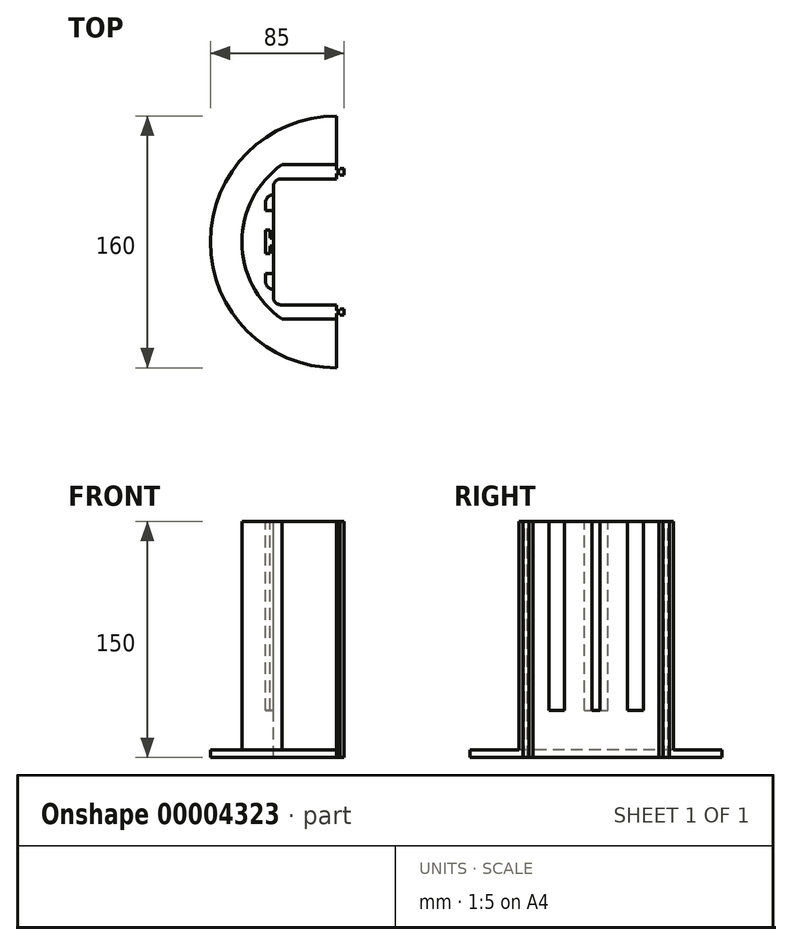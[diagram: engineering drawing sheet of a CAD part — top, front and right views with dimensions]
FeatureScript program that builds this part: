
annotation { "Feature Type Name" : "Feature", "Feature Type Description" : "" }
export const myFeature = defineFeature(function(context is Context, id is Id, definition is map)
    precondition{}
    {
        {
            var Q0;
            Q0=qCreatedBy(makeId("Top.planeOp"),FACE);
            var sketch = newSketch(context, id + "F0", { "sketchPlane" : qUnion([Q0])});
            skArc(sketch, "E0", {"start": v(0, 80) * mm, "mid": v(-80, 0) * mm, "end": v(0, -80) * mm});
            skLineSegment(sketch, "E1", {"start": v(0, -80) * mm, "end": v(0, 80) * mm});
            skLineSegment(sketch, "E2.0", {"start": v(-40, -35) * mm, "end": v(-40, 35) * mm});
            skLineSegment(sketch, "E3", {"start": v(-40, -80) * mm, "end": v(0, -80) * mm});
            skLineSegment(sketch, "E4.2", {"start": v(-43.15, -34.71) * mm, "end": v(-43.15, -34.34) * mm});
            skPoint(sketch, "E5.orphan", {"position": v(0, 60) * mm});
            skLineSegment(sketch, "E6.trimOffspring", {"start": v(-43.15, 34.91) * mm, "end": v(-43.15, 35.29) * mm});
            skLineSegment(sketch, "E7.0", {"start": v(-35, -40) * mm, "end": v(0, -40) * mm});
            skLineSegment(sketch, "E8.0", {"start": v(-35, -49) * mm, "end": v(0, -49) * mm});
            skArc(sketch, "E9.0", {"start": v(-34.63, 49) * mm, "mid": v(-60, 0) * mm, "end": v(-34.63, -49) * mm});
            skLineSegment(sketch, "E10.0", {"start": v(0, 40) * mm, "end": v(-35, 40) * mm});
            skLineSegment(sketch, "E11.0", {"start": v(0, 49) * mm, "end": v(-35, 49) * mm});
            skPoint(sketch, "E12.visualSharp", {"position": v(-40, 40) * mm});
            skArc(sketch, "E12.filletArc", {"start": v(-35, 40) * mm, "mid": v(-38.54, 38.54) * mm, "end": v(-40, 35) * mm});
            skPoint(sketch, "E13.visualSharp", {"position": v(-40, -40) * mm});
            skArc(sketch, "E13.filletArc", {"start": v(-40, -35) * mm, "mid": v(-38.54, -38.54) * mm, "end": v(-35, -40) * mm});
            skSolve(sketch);
        }
        {
            var Q0;
            {var subQ5=sQuery(id+"F0.wireOp",EDGE,"75c2bebc-5728-42c0-99f1-8c9a0116536a.0");Q0=makeQuery(id+"F0.imprint","IMPRINT",FACE,{"disambiguationData":[TD([[makeQuery(id+"F0.imprint","IMPRINT",EDGE,{"derivedFrom":subQ5}),-1.0]])]});}
            var Q1;
            {var subQ1=sQuery(id+"F0.wireOp",EDGE,"E2.0");var subQ5=makeQuery(id+"F0.imprint","INTERSECT",VERTEX,{"derivedFrom":[subQ1,sQuery(id+"F0.wireOp",EDGE,"75c2bebc-5728-42c0-99f1-8c9a0116536a.0")]});Q1=makeQuery(id+"F0.imprint","IMPRINT",FACE,{"disambiguationData":[TD([[makeQuery(id+"F0.imprint","IMPRINT",EDGE,{"disambiguationData":[TD([[subQ5,1.0]])],"derivedFrom":subQ1}),1.0]])]});}
            var Q2;
            {var subQ0=sQuery(id+"F0.wireOp",EDGE,"6f7f12fe-7da2-44be-81c8-f102f9fe9926.0");Q2=makeQuery(id+"F0.imprint","IMPRINT",FACE,{"disambiguationData":[TD([[makeQuery(id+"F0.imprint","IMPRINT",EDGE,{"derivedFrom":subQ0}),-1.0]])]});}
            extrude(context, id + "F1", {"entities" : qUnion([Q0, Q1, Q2]), "oppositeDirection" : true, "depth" : 150 * mm});
        }
        {
            var Q0;
            Q0=makeQuery(id+"F1.opExtrude","CAP_FACE",FACE,{"disambiguationData":[OSD([sQuery(id+"F0.wireOp",EDGE,"E1"),sQuery(id+"F0.wireOp",EDGE,"E2.0"),sQuery(id+"F0.wireOp",EDGE,"75c2bebc-5728-42c0-99f1-8c9a0116536a.0"),sQuery(id+"F0.wireOp",EDGE,"6f7f12fe-7da2-44be-81c8-f102f9fe9926.0"),sQuery(id+"F0.wireOp",EDGE,"6ea0f182-5685-4d39-b26f-b4a1ce07e50b.0")])],"isStart":false});
            var sketch = newSketch(context, id + "F2", { "sketchPlane" : qUnion([Q0])});
            skLineSegment(sketch, "E14", {"start": v(0, 40) * mm, "end": v(0, -80) * mm});
            skLineSegment(sketch, "E15", {"start": v(0, 40) * mm, "end": v(0, 80) * mm});
            skArc(sketch, "E16", {"start": v(0, 80) * mm, "mid": v(-80, 0) * mm, "end": v(0, -80) * mm});
            skSolve(sketch);
        }
        {
            var Q0;
            {var subQ2=sQuery(id+"F2.wireOp",EDGE,"E16");Q0=makeQuery(id+"F2.imprint","IMPRINT",FACE,{"disambiguationData":[TD([[makeQuery(id+"F2.imprint","IMPRINT",EDGE,{"derivedFrom":subQ2}),1.0]])]});}
            extrude(context, id + "F3", {"entities" : qUnion([Q0]), "operationType" : NewBodyOperationType.ADD, "oppositeDirection" : true, "depth" : 5 * mm});
        }
        {
            var Q0;
            Q0=makeQuery(id+"F1.opExtrude","CAP_FACE",FACE,{"disambiguationData":[OSD([sQuery(id+"F0.wireOp",EDGE,"E1"),sQuery(id+"F0.wireOp",EDGE,"E2.0"),sQuery(id+"F0.wireOp",EDGE,"75c2bebc-5728-42c0-99f1-8c9a0116536a.0"),sQuery(id+"F0.wireOp",EDGE,"6f7f12fe-7da2-44be-81c8-f102f9fe9926.0"),sQuery(id+"F0.wireOp",EDGE,"6ea0f182-5685-4d39-b26f-b4a1ce07e50b.0"),sQuery(id+"F0.wireOp",EDGE,"e7ebfef1-af54-467c-9f28-ac26729f73ad.filletArc"),sQuery(id+"F0.wireOp",EDGE,"8241e0cd-7dbd-4ec0-b380-70d9f552f549.filletArc")])],"isStart":true});
            var sketch = newSketch(context, id + "F4", { "sketchPlane" : qUnion([Q0])});
            skLineSegment(sketch, "E17", {"start": v(0, -40) * mm, "end": v(5, -40) * mm});
            skLineSegment(sketch, "E18", {"start": v(0, 40) * mm, "end": v(5, 40) * mm});
            skLineSegment(sketch, "E19.0", {"start": v(0, 43.5) * mm, "end": v(2.5, 43.5) * mm});
            skLineSegment(sketch, "E20.0", {"start": v(0, 45.5) * mm, "end": v(2.5, 45.5) * mm});
            skLineSegment(sketch, "E21", {"start": v(5, 45.5) * mm, "end": v(5, 43.5) * mm});
            skLineSegment(sketch, "E22.0", {"start": v(0, 45.5) * mm, "end": v(0, 43.5) * mm});
            skLineSegment(sketch, "E23", {"start": v(5, 45.5) * mm, "end": v(5, 46.5) * mm});
            skLineSegment(sketch, "E24", {"start": v(5, 43.5) * mm, "end": v(5, 42.5) * mm});
            skLineSegment(sketch, "E25.0", {"start": v(2.5, 45.5) * mm, "end": v(2.5, 46.5) * mm});
            skLineSegment(sketch, "E25.2", {"start": v(2.5, 43.5) * mm, "end": v(2.5, 42.5) * mm});
            skLineSegment(sketch, "E26", {"start": v(5, 42.5) * mm, "end": v(2.5, 42.5) * mm});
            skLineSegment(sketch, "E27", {"start": v(2.5, 46.5) * mm, "end": v(5, 46.5) * mm});
            skLineSegment(sketch, "E28.0", {"start": v(0, -45.5) * mm, "end": v(2.5, -45.5) * mm});
            skLineSegment(sketch, "E29.0", {"start": v(0, -43.5) * mm, "end": v(2.5, -43.5) * mm});
            skLineSegment(sketch, "E30", {"start": v(5, -43.5) * mm, "end": v(5, -45.5) * mm});
            skLineSegment(sketch, "E31", {"start": v(5, -43.5) * mm, "end": v(5, -42.5) * mm});
            skLineSegment(sketch, "E32", {"start": v(5, -45.5) * mm, "end": v(5, -46.5) * mm});
            skLineSegment(sketch, "E33.0", {"start": v(2.5, -43.5) * mm, "end": v(2.5, -42.5) * mm});
            skLineSegment(sketch, "E33.2", {"start": v(2.5, -45.5) * mm, "end": v(2.5, -46.5) * mm});
            skLineSegment(sketch, "E34", {"start": v(5, -42.5) * mm, "end": v(2.5, -42.5) * mm});
            skLineSegment(sketch, "E35", {"start": v(5, -46.5) * mm, "end": v(2.5, -46.5) * mm});
            skSolve(sketch);
        }
        {
            var Q0;
            Q0=makeQuery(id+"F4.imprint","IMPRINT",FACE,{"disambiguationData":[TD([[makeQuery(id+"F4.imprint","IMPRINT",EDGE,{"derivedFrom":sQuery(id+"F4.wireOp",EDGE,"E19.0")}),1.0]])]});
            var Q1;
            {var subQ3=sQuery(id+"F4.wireOp",EDGE,"E28.0");Q1=makeQuery(id+"F4.imprint","IMPRINT",FACE,{"disambiguationData":[TD([[makeQuery(id+"F4.imprint","IMPRINT",EDGE,{"derivedFrom":subQ3}),1.0]])]});}
            extrude(context, id + "F5", {"entities" : qUnion([Q0, Q1]), "operationType" : NewBodyOperationType.ADD, "oppositeDirection" : true, "depth" : 150 * mm});
        }
        {
            var Q0;
            {var subQ0=sQuery(id+"F0.wireOp",EDGE,"E1");Q0=makeQuery(id+"F5.boolean.opBoolean","MERGE",FACE,{"derivedFrom":[makeQuery(id+"F1.opExtrude","CAP_FACE",FACE,{"disambiguationData":[OSD([subQ0,sQuery(id+"F0.wireOp",EDGE,"E2.0"),sQuery(id+"F0.wireOp",EDGE,"75c2bebc-5728-42c0-99f1-8c9a0116536a.0"),sQuery(id+"F0.wireOp",EDGE,"6f7f12fe-7da2-44be-81c8-f102f9fe9926.0"),sQuery(id+"F0.wireOp",EDGE,"6ea0f182-5685-4d39-b26f-b4a1ce07e50b.0"),sQuery(id+"F0.wireOp",EDGE,"e7ebfef1-af54-467c-9f28-ac26729f73ad.filletArc"),sQuery(id+"F0.wireOp",EDGE,"8241e0cd-7dbd-4ec0-b380-70d9f552f549.filletArc")])],"isStart":true}),makeQuery(id+"F5.opExtrude","CAP_FACE",FACE,{"disambiguationData":[OSD([sQuery(id+"F4.wireOp",EDGE,"afc29b5e-58cc-4c7b-a192-24bd55086143.0"),sQuery(id+"F4.wireOp",EDGE,"29f716cb-9728-41fc-a06d-da8974d49b97.0"),sQuery(id+"F4.wireOp",EDGE,"28a342e1-f6da-4660-be7d-c49b4d0e2a07"),sQuery(id+"F4.wireOp",EDGE,"23a93fd6-abec-4492-8de1-6d2303d71052.0"),sQuery(id+"F4.wireOp",EDGE,"97a3bef3-9aef-4252-a859-6bd18b588f87"),sQuery(id+"F4.wireOp",EDGE,"a65524c8-dac2-4c7d-890a-83aa3edf8c0d"),sQuery(id+"F4.wireOp",EDGE,"3f23ce79-a299-4ef1-861a-d1ed6e96b0e4.0"),sQuery(id+"F4.wireOp",EDGE,"20cd2892-1dbe-4ddd-b802-98d3355a453f.0"),sQuery(id+"F4.wireOp",EDGE,"12dbb6a1-9dd6-4ab8-8469-4905e3c74d78"),sQuery(id+"F4.wireOp",EDGE,"0f2de19d-25e8-473d-b9a4-17b5fc715538")])],"isStart":true}),makeQuery(id+"F5.opExtrude","CAP_FACE",FACE,{"disambiguationData":[OSD([subQ0,sQuery(id+"F4.wireOp",EDGE,"73ee2f29-bcec-40ac-88de-c9b1e0e0407e.0"),sQuery(id+"F4.wireOp",EDGE,"760f6a40-cbb3-4914-97d4-89d93c9b81f9.0"),sQuery(id+"F4.wireOp",EDGE,"a534df8f-d272-4bc9-bed5-e4d40ce864a1"),sQuery(id+"F4.wireOp",EDGE,"6b7fad69-a33e-43b3-a84d-1ef3c3cb7823"),sQuery(id+"F4.wireOp",EDGE,"69421ab4-d4ba-4d9a-9d42-b271e840dfdb"),sQuery(id+"F4.wireOp",EDGE,"92609034-8b91-410d-badb-3a131ae02ed0.0"),sQuery(id+"F4.wireOp",EDGE,"3dc5bcb1-a6b0-4089-b62b-5cdfe9c19cc5.0"),sQuery(id+"F4.wireOp",EDGE,"abeddcaf-58ac-4aa6-872a-ad95cb22dacf"),sQuery(id+"F4.wireOp",EDGE,"0830cdb0-8186-4697-8fae-c01160b7307a")])],"isStart":true})]});}
            var sketch = newSketch(context, id + "F6", { "sketchPlane" : qUnion([Q0])});
            skLineSegment(sketch, "E36.0", {"start": v(-40, 2.5) * mm, "end": v(-42, 2.5) * mm});
            skLineSegment(sketch, "E37.0", {"start": v(-40, -2.5) * mm, "end": v(-42, -2.5) * mm});
            skLineSegment(sketch, "E38", {"start": v(-40, -2.5) * mm, "end": v(-40, 2.5) * mm});
            skLineSegment(sketch, "E39.0", {"start": v(-42, 2.5) * mm, "end": v(-42, 7.5) * mm});
            skLineSegment(sketch, "E40", {"start": v(-45, 7.5) * mm, "end": v(-42, 7.5) * mm});
            skLineSegment(sketch, "E41.0", {"start": v(-42, -2.5) * mm, "end": v(-42, -7.5) * mm});
            skLineSegment(sketch, "E42", {"start": v(-45, -7.5) * mm, "end": v(-42, -7.5) * mm});
            skLineSegment(sketch, "E43.0", {"start": v(-45, -2.5) * mm, "end": v(-45, 7.5) * mm});
            skLineSegment(sketch, "E44.0", {"start": v(-45, -2.5) * mm, "end": v(-45, -7.5) * mm});
            skSolve(sketch);
        }
        {
            var Q0;
            Q0=makeQuery(id+"F6.imprint","IMPRINT",FACE,{"disambiguationData":[TD([[makeQuery(id+"F6.imprint","IMPRINT",EDGE,{"derivedFrom":sQuery(id+"F6.wireOp",EDGE,"E36.0")}),1.0]])]});
            extrude(context, id + "F7", {"entities" : qUnion([Q0]), "operationType" : NewBodyOperationType.REMOVE, "oppositeDirection" : true, "depth" : 120 * mm});
        }
        {
            var Q0;
            {var subQ0=sQuery(id+"F0.wireOp",EDGE,"E1");Q0=makeQuery(id+"F5.boolean.opBoolean","MERGE",FACE,{"derivedFrom":[makeQuery(id+"F1.opExtrude","CAP_FACE",FACE,{"disambiguationData":[OSD([subQ0,sQuery(id+"F0.wireOp",EDGE,"E2.0"),sQuery(id+"F0.wireOp",EDGE,"E7.0"),sQuery(id+"F0.wireOp",EDGE,"E8.0"),sQuery(id+"F0.wireOp",EDGE,"E9.0"),sQuery(id+"F0.wireOp",EDGE,"E10.0"),sQuery(id+"F0.wireOp",EDGE,"E11.0"),sQuery(id+"F0.wireOp",EDGE,"E12.filletArc"),sQuery(id+"F0.wireOp",EDGE,"E13.filletArc")])],"isStart":true}),makeQuery(id+"F5.opExtrude","CAP_FACE",FACE,{"disambiguationData":[OSD([sQuery(id+"F4.wireOp",EDGE,"E19.0"),sQuery(id+"F4.wireOp",EDGE,"E20.0"),sQuery(id+"F4.wireOp",EDGE,"E21"),sQuery(id+"F4.wireOp",EDGE,"E22.0"),sQuery(id+"F4.wireOp",EDGE,"E23"),sQuery(id+"F4.wireOp",EDGE,"E24"),sQuery(id+"F4.wireOp",EDGE,"E25.0"),sQuery(id+"F4.wireOp",EDGE,"E25.2"),sQuery(id+"F4.wireOp",EDGE,"E26"),sQuery(id+"F4.wireOp",EDGE,"E27")])],"isStart":true}),makeQuery(id+"F5.opExtrude","CAP_FACE",FACE,{"disambiguationData":[OSD([subQ0,sQuery(id+"F4.wireOp",EDGE,"E28.0"),sQuery(id+"F4.wireOp",EDGE,"E29.0"),sQuery(id+"F4.wireOp",EDGE,"E30"),sQuery(id+"F4.wireOp",EDGE,"E31"),sQuery(id+"F4.wireOp",EDGE,"E32"),sQuery(id+"F4.wireOp",EDGE,"E33.0"),sQuery(id+"F4.wireOp",EDGE,"E33.2"),sQuery(id+"F4.wireOp",EDGE,"E34"),sQuery(id+"F4.wireOp",EDGE,"E35")])],"isStart":true})]});}
            var sketch = newSketch(context, id + "F8", { "sketchPlane" : qUnion([Q0])});
            skLineSegment(sketch, "E45.0", {"start": v(-40, 20) * mm, "end": v(-40, 20) * mm});
            skLineSegment(sketch, "E46.0", {"start": v(-40, 35) * mm, "end": v(-40, 35) * mm});
            skLineSegment(sketch, "E47.0", {"start": v(-40, -35) * mm, "end": v(-40, -35) * mm});
            skLineSegment(sketch, "E48.0", {"start": v(-40, -20) * mm, "end": v(-40, -20) * mm});
            skLineSegment(sketch, "E49", {"start": v(-40, 30) * mm, "end": v(-40, -30) * mm});
            skLineSegment(sketch, "E50.0", {"start": v(-45, -20) * mm, "end": v(-45, -25) * mm});
            skLineSegment(sketch, "E51", {"start": v(-45, 25) * mm, "end": v(-45, 20) * mm});
            skPoint(sketch, "E52.visualSharp", {"position": v(-45, 20) * mm});
            skPoint(sketch, "E53.visualSharp", {"position": v(-45, 35) * mm});
            skLineSegment(sketch, "E54", {"start": v(-40, -30) * mm, "end": v(-40, -30) * mm});
            skLineSegment(sketch, "E55", {"start": v(-40, 30) * mm, "end": v(-40, 30) * mm});
            skLineSegment(sketch, "E56", {"start": v(-40, -20) * mm, "end": v(-45, -20) * mm});
            skPoint(sketch, "E57.orphan", {"position": v(-45, -25) * mm});
            skPoint(sketch, "E58.visualSharp", {"position": v(-45, -30) * mm});
            skArc(sketch, "E58.filletArc", {"start": v(-45, -25) * mm, "mid": v(-43.54, -28.54) * mm, "end": v(-40, -30) * mm});
            skLineSegment(sketch, "E59", {"start": v(-40, 20) * mm, "end": v(-45, 20) * mm});
            skPoint(sketch, "E60.visualSharp", {"position": v(-45, 30) * mm});
            skArc(sketch, "E60.filletArc", {"start": v(-40, 30) * mm, "mid": v(-43.54, 28.54) * mm, "end": v(-45, 25) * mm});
            skSolve(sketch);
        }
        {
            var Q0;
            Q0=makeQuery(id+"F8.imprint","IMPRINT",FACE,{"disambiguationData":[TD([[makeQuery(id+"F8.imprint","IMPRINT",EDGE,{"derivedFrom":sQuery(id+"F8.wireOp",EDGE,"E51")}),1.0]])]});
            var Q1;
            Q1=makeQuery(id+"F8.imprint","IMPRINT",FACE,{"disambiguationData":[TD([[makeQuery(id+"F8.imprint","IMPRINT",EDGE,{"derivedFrom":sQuery(id+"F8.wireOp",EDGE,"E50.0")}),1.0]])]});
            extrude(context, id + "F9", {"entities" : qUnion([Q0, Q1]), "operationType" : NewBodyOperationType.REMOVE, "oppositeDirection" : true, "depth" : 120 * mm});
        }
    });
